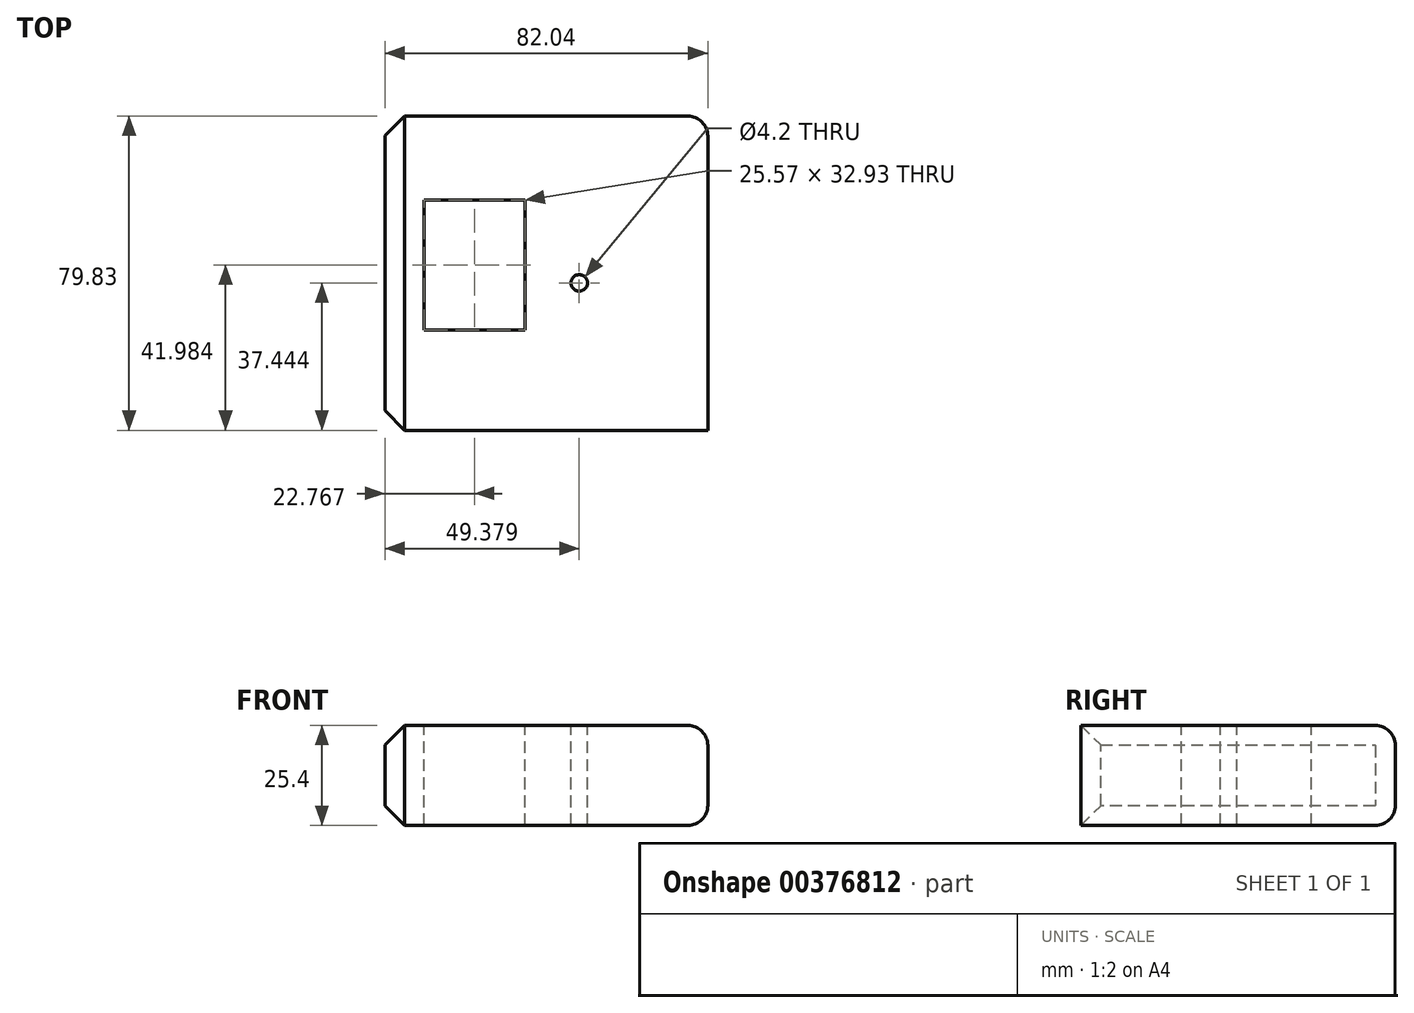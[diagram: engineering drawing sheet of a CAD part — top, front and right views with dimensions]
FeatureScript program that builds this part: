
annotation { "Feature Type Name" : "Feature", "Feature Type Description" : "" }
export const myFeature = defineFeature(function(context is Context, id is Id, definition is map)
    precondition{}
    {
        {
            var Q0;
            Q0=qCreatedBy(makeId("Top.planeOp"),FACE);
            var sketch = newSketch(context, id + "F0", { "sketchPlane" : qUnion([Q0])});
            skLineSegment(sketch, "E0.bottom", {"start": v(0, 0) * mm, "end": v(82.04, 0) * mm});
            skLineSegment(sketch, "E0.top", {"start": v(0, 79.83) * mm, "end": v(82.04, 79.83) * mm});
            skLineSegment(sketch, "E0.left", {"start": v(0, 0) * mm, "end": v(0, 79.83) * mm});
            skLineSegment(sketch, "E0.right", {"start": v(82.04, 0) * mm, "end": v(82.04, 79.83) * mm});
            skSolve(sketch);
        }
        {
            var Q0;
            Q0=makeQuery(id+"F0.imprint","IMPRINT",FACE,{"disambiguationData":[TD([[makeQuery(id+"F0.imprint","IMPRINT",EDGE,{"derivedFrom":sQuery(id+"F0.wireOp",EDGE,"E0.bottom")}),1.0]])]});
            extrude(context, id + "F1", {"entities" : qUnion([Q0]), "depth" : 25.4 * mm});
        }
        {
            var Q0;
            Q0=makeQuery(id+"F1.opExtrude","CAP_FACE",FACE,{"disambiguationData":[OSD([sQuery(id+"F0.wireOp",EDGE,"E0.bottom"),sQuery(id+"F0.wireOp",EDGE,"E0.top"),sQuery(id+"F0.wireOp",EDGE,"E0.left"),sQuery(id+"F0.wireOp",EDGE,"E0.right")])],"isStart":false});
            var sketch = newSketch(context, id + "F2", { "sketchPlane" : qUnion([Q0])});
            skPoint(sketch, "E1", {"position": v(49.38, 37.44) * mm});
            skSolve(sketch);
        }
        {
            var Q0;
            Q0=sQuery(id+"F2.wireOp",VERTEX,"E1");
            var Q1;
            Q1=makeQuery(id+"F1.opExtrude","SWEPT_BODY",BODY,{"disambiguationData":[OSD([sQuery(id+"F0.wireOp",EDGE,"E0.bottom"),sQuery(id+"F0.wireOp",EDGE,"E0.top"),sQuery(id+"F0.wireOp",EDGE,"E0.left"),sQuery(id+"F0.wireOp",EDGE,"E0.right")])]});
            hole(context, id + "F3", {"style" : HoleStyle.SIMPLE, "endStyle" : HoleEndStyle.THROUGH, "standardTappedOrClearance" : lookupTablePath({ "standard" : "ISO", "engagement" : "75%", "pitch" : "0.8 mm", "size" : "M5", "type" : "Tapped" }), "standardBlindInLast" : lookupTablePath({ "standard" : "ISO", "engagement" : "75%", "pitch" : "0.8 mm", "size" : "M5", "type" : "Tapped" }), "holeDiameter" : 4.2 * mm, "showTappedDepth" : true, "isTappedThrough" : true, "tappedDepth" : 12.7 * mm, "tapClearance" : 3, "locations" : qUnion([Q0]), "scope" : qUnion([Q1]), "majorDiameter" : 5 * mm});
        }
        {
            var Q0;
            Q0=makeQuery(id+"F1.opExtrude","SWEPT_EDGE",EDGE,{"disambiguationData":[OSD([sQuery(id+"F0.wireOp",EDGE,"E0.top"),sQuery(id+"F0.wireOp",EDGE,"E0.right")])]});
            fillet(context, id + "F4", {"entities" : qUnion([Q0]), "radius" : 5.08 * mm, "tangentPropagation" : true, "allowEdgeOverflow" : false});
        }
        {
            var Q0;
            Q0=makeQuery(id+"F1.opExtrude","CAP_EDGE",EDGE,{"disambiguationData":[OSD([sQuery(id+"F0.wireOp",EDGE,"E0.right")])],"isStart":true});
            fillet(context, id + "F5", {"entities" : qUnion([Q0]), "radius" : 5.08 * mm, "tangentPropagation" : true, "allowEdgeOverflow" : false});
        }
        {
            var Q0;
            Q0=makeQuery(id+"F1.opExtrude","CAP_EDGE",EDGE,{"disambiguationData":[OSD([sQuery(id+"F0.wireOp",EDGE,"E0.top")])],"isStart":false});
            fillet(context, id + "F6", {"entities" : qUnion([Q0]), "radius" : 5.08 * mm, "tangentPropagation" : true, "allowEdgeOverflow" : false});
        }
        {
            var Q0;
            Q0=makeQuery(id+"F1.opExtrude","CAP_FACE",FACE,{"disambiguationData":[OSD([sQuery(id+"F0.wireOp",EDGE,"E0.bottom"),sQuery(id+"F0.wireOp",EDGE,"E0.top"),sQuery(id+"F0.wireOp",EDGE,"E0.left"),sQuery(id+"F0.wireOp",EDGE,"E0.right")])],"isStart":false});
            var sketch = newSketch(context, id + "F7", { "sketchPlane" : qUnion([Q0])});
            skLineSegment(sketch, "E2.bottom", {"start": v(35.55, 25.52) * mm, "end": v(9.98, 25.52) * mm});
            skLineSegment(sketch, "E2.top", {"start": v(35.55, 58.45) * mm, "end": v(9.98, 58.45) * mm});
            skLineSegment(sketch, "E2.left", {"start": v(35.55, 25.52) * mm, "end": v(35.55, 58.45) * mm});
            skLineSegment(sketch, "E2.right", {"start": v(9.98, 25.52) * mm, "end": v(9.98, 58.45) * mm});
            skSolve(sketch);
        }
        {
            var Q0;
            Q0=qSketchRegion(id+"F7",true);
            extrude(context, id + "F8", {"entities" : qUnion([Q0]), "operationType" : NewBodyOperationType.REMOVE, "oppositeDirection" : true, "depth" : 25.4 * mm});
        }
        {
            var Q0;
            Q0=makeQuery(id+"F1.opExtrude","SWEPT_FACE",FACE,{"disambiguationData":[OSD([sQuery(id+"F0.wireOp",EDGE,"E0.left")])]});
            chamfer(context, id + "F9", {"entities" : qUnion([Q0]), "width" : 5 * mm, "tangentPropagation" : true});
        }
    });
